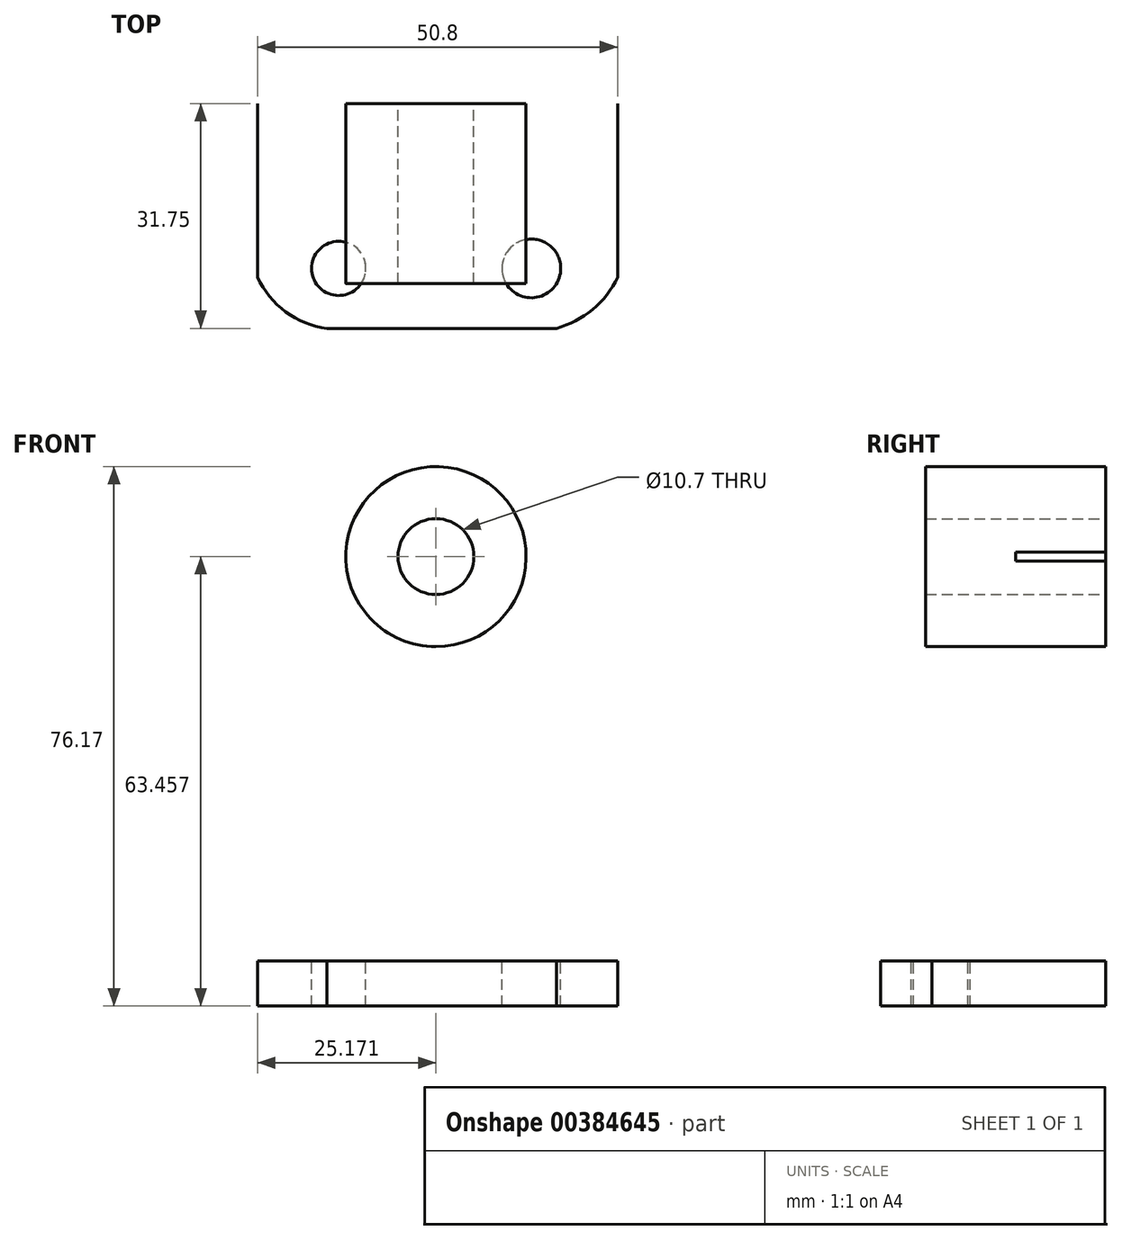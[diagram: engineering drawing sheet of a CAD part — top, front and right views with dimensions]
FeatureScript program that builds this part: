
annotation { "Feature Type Name" : "Feature", "Feature Type Description" : "" }
export const myFeature = defineFeature(function(context is Context, id is Id, definition is map)
    precondition{}
    {
        {
            var Q0;
            Q0=qCreatedBy(makeId("Front.planeOp"),FACE);
            var sketch = newSketch(context, id + "F0", { "sketchPlane" : qUnion([Q0])});
            skLineSegment(sketch, "E0", {"start": v(-22.79, 0) * mm, "end": v(-22.79, 6.35) * mm});
            skLineSegment(sketch, "E1", {"start": v(-22.79, 6.35) * mm, "end": v(28.01, 6.35) * mm});
            skLineSegment(sketch, "E2", {"start": v(28.01, 6.35) * mm, "end": v(28.01, 0) * mm});
            skLineSegment(sketch, "E3", {"start": v(28.01, 0) * mm, "end": v(-22.79, 0) * mm});
            skSolve(sketch);
        }
        {
            var Q0;
            Q0=makeQuery(id+"F0.imprint","IMPRINT",FACE,{"disambiguationData":[TD([[makeQuery(id+"F0.imprint","IMPRINT",EDGE,{"derivedFrom":sQuery(id+"F0.wireOp",EDGE,"E0")}),-1.0]])]});
            extrude(context, id + "F1", {"entities" : qUnion([Q0]), "depth" : 31.75 * mm});
        }
        {
            var Q0;
            Q0=makeQuery(id+"F1.opExtrude","SWEPT_FACE",FACE,{"disambiguationData":[OSD([sQuery(id+"F0.wireOp",EDGE,"E1")])]});
            var sketch = newSketch(context, id + "F2", { "sketchPlane" : qUnion([Q0])});
            skLineSegment(sketch, "E4", {"start": v(28.01, -12.7) * mm, "end": v(-22.79, -12.7) * mm});
            skLineSegment(sketch, "E5", {"start": v(-22.79, -12.7) * mm, "end": v(-22.79, 0) * mm});
            skLineSegment(sketch, "E6", {"start": v(-22.79, 0) * mm, "end": v(28.01, 0) * mm});
            skLineSegment(sketch, "E7", {"start": v(28.01, 0) * mm, "end": v(28.01, -12.7) * mm});
            skSolve(sketch);
        }
        {
            var Q0;
            Q0=makeQuery(id+"F2.imprint","IMPRINT",FACE,{"disambiguationData":[TD([[makeQuery(id+"F2.imprint","IMPRINT",EDGE,{"derivedFrom":sQuery(id+"F2.wireOp",EDGE,"E4")}),-1.0]])]});
            extrude(context, id + "F3", {"entities" : qUnion([Q0]), "operationType" : NewBodyOperationType.ADD, "depth" : 69.85 * mm});
        }
        {
            var Q0;
            Q0=makeQuery(id+"F1.opExtrude","SWEPT_FACE",FACE,{"disambiguationData":[OSD([sQuery(id+"F0.wireOp",EDGE,"E1")])]});
            var sketch = newSketch(context, id + "F4", { "sketchPlane" : qUnion([Q0])});
            skArc(sketch, "E8", {"start": v(-22.79, -24.5) * mm, "mid": v(-18.82, -29.4) * mm, "end": v(-12.97, -31.75) * mm});
            skArc(sketch, "E9", {"start": v(19.36, -31.75) * mm, "mid": v(24.48, -29.08) * mm, "end": v(28.01, -24.5) * mm});
            skCircle(sketch, "E10", {"center": v(15.85, -23.28) * mm, "radius": 4.15 * mm});
            skCircle(sketch, "E11", {"center": v(-11.33, -23.28) * mm, "radius": 3.83 * mm});
            skSolve(sketch);
        }
        {
            var Q0;
            Q0 = qSketchRegion(id + "F4", true);
            var Q1;
            {var subQ0=sQuery(id+"F4.wireOp",EDGE,"E8");Q1=makeQuery(id+"F4.imprint","IMPRINT",FACE,{"disambiguationData":[TD([[makeQuery(id+"F4.imprint","IMPRINT",EDGE,{"derivedFrom":subQ0}),-1.0]])]});}
            var Q2;
            {var subQ0=sQuery(id+"F4.wireOp",EDGE,"E9");Q2=makeQuery(id+"F4.imprint","IMPRINT",FACE,{"disambiguationData":[TD([[makeQuery(id+"F4.imprint","IMPRINT",EDGE,{"derivedFrom":subQ0}),-1.0]])]});}
            extrude(context, id + "F5", {"entities" : qUnion([Q0, Q1, Q2]), "operationType" : NewBodyOperationType.REMOVE, "oppositeDirection" : true, "depth" : 12.7 * mm});
        }
        {
            var Q0;
            Q0=makeQuery(id+"F3.opExtrude","SWEPT_FACE",FACE,{"disambiguationData":[OSD([sQuery(id+"F2.wireOp",EDGE,"E4")])]});
            var sketch = newSketch(context, id + "F6", { "sketchPlane" : qUnion([Q0])});
            skArc(sketch, "E12", {"start": v(-22.79, 6.35) * mm, "mid": v(-13.83, 12.96) * mm, "end": v(-10.32, 23.53) * mm});
            skArc(sketch, "E13", {"start": v(15.08, 23.53) * mm, "mid": v(19.1, 13.1) * mm, "end": v(28.01, 6.35) * mm});
            skLineSegment(sketch, "E14", {"start": v(-10.32, 23.53) * mm, "end": v(-10.32, 76.2) * mm});
            skLineSegment(sketch, "E15", {"start": v(-10.32, 76.2) * mm, "end": v(15.08, 76.2) * mm});
            skLineSegment(sketch, "E16", {"start": v(15.08, 76.2) * mm, "end": v(15.08, 23.53) * mm});
            skSolve(sketch);
        }
        {
            var Q0;
            Q0 = qSketchRegion(id + "F6", true);
            var Q1;
            Q1=makeQuery(id+"F6.imprint","IMPRINT",FACE,{"disambiguationData":[TD([[makeQuery(id+"F6.imprint","IMPRINT",EDGE,{"derivedFrom":sQuery(id+"F6.wireOp",EDGE,"E12")}),1.0]])]});
            var Q2;
            Q2=makeQuery(id+"F6.imprint","IMPRINT",FACE,{"disambiguationData":[TD([[makeQuery(id+"F6.imprint","IMPRINT",EDGE,{"derivedFrom":sQuery(id+"F6.wireOp",EDGE,"E13")}),1.0]])]});
            extrude(context, id + "F7", {"entities" : qUnion([Q0, Q1, Q2]), "operationType" : NewBodyOperationType.REMOVE, "oppositeDirection" : true, "depth" : 12.7 * mm});
        }
        {
            var Q0;
            Q0=makeQuery(id+"F3.opExtrude","SWEPT_FACE",FACE,{"disambiguationData":[OSD([sQuery(id+"F2.wireOp",EDGE,"E4")])]});
            var sketch = newSketch(context, id + "F8", { "sketchPlane" : qUnion([Q0])});
            skCircle(sketch, "E17", {"center": v(2.38, 63.46) * mm, "radius": 12.72 * mm});
            skPoint(sketch, "E17.centerSnap0", {"position": v(2.38, 76.2) * mm});
            skCircle(sketch, "E18", {"center": v(2.38, 63.46) * mm, "radius": 5.35 * mm});
            skSolve(sketch);
        }
        {
            var Q0;
            Q0=makeQuery(id+"F8.imprint","IMPRINT",FACE,{"disambiguationData":[TD([[makeQuery(id+"F8.imprint","IMPRINT",EDGE,{"derivedFrom":sQuery(id+"F8.wireOp",EDGE,"E18")}),-1.0]])]});
            extrude(context, id + "F9", {"entities" : qUnion([Q0]), "operationType" : NewBodyOperationType.ADD, "depth" : 12.7 * mm});
        }
        {
            var Q0;
            {var subQ0=sQuery(id+"F6.wireOp",EDGE,"E14");var subQ1=sQuery(id+"F8.wireOp",EDGE,"E17");var subQ3=sQuery(id+"F2.wireOp",EDGE,"E4");Q0=makeQuery(id+"F9.boolean.opBoolean","SPLIT",FACE,{"disambiguationData":[TD([makeQuery(id+"F9.opExtrude","SWEPT_FACE",FACE,{"disambiguationData":[OSD([subQ1]),TDD([makeQuery(id+"F8.imprint","IMPRINT",EDGE,{"disambiguationData":[TD([[makeQuery(id+"F8.imprint","INTERSECT",VERTEX,{"disambiguationData":[OD(0.0)],"derivedFrom":[makeQuery(id+"F7.boolean.opBoolean","COPY",EDGE,{"derivedFrom":makeQuery(id+"F7.opExtrude","CAP_EDGE",EDGE,{"disambiguationData":[OSD([subQ0])],"isStart":true})}),subQ1]}),1.0]])],"derivedFrom":subQ1})])]})])],"derivedFrom":makeQuery(id+"F3.opExtrude","SWEPT_FACE",FACE,{"disambiguationData":[OSD([subQ3])]})});}
            var Q1;
            Q1=makeQuery(id+"F9.boolean.opBoolean","SPLIT",FACE,{"disambiguationData":[TD([makeQuery(id+"F9.opExtrude","SWEPT_FACE",FACE,{"disambiguationData":[OSD([sQuery(id+"F8.wireOp",EDGE,"E18")])]})])],"derivedFrom":makeQuery(id+"F3.opExtrude","SWEPT_FACE",FACE,{"disambiguationData":[OSD([sQuery(id+"F2.wireOp",EDGE,"E4")])]})});
            extrude(context, id + "F10", {"entities" : qUnion([Q0, Q1]), "operationType" : NewBodyOperationType.REMOVE, "oppositeDirection" : true, "depth" : 12.7 * mm});
        }
    });
